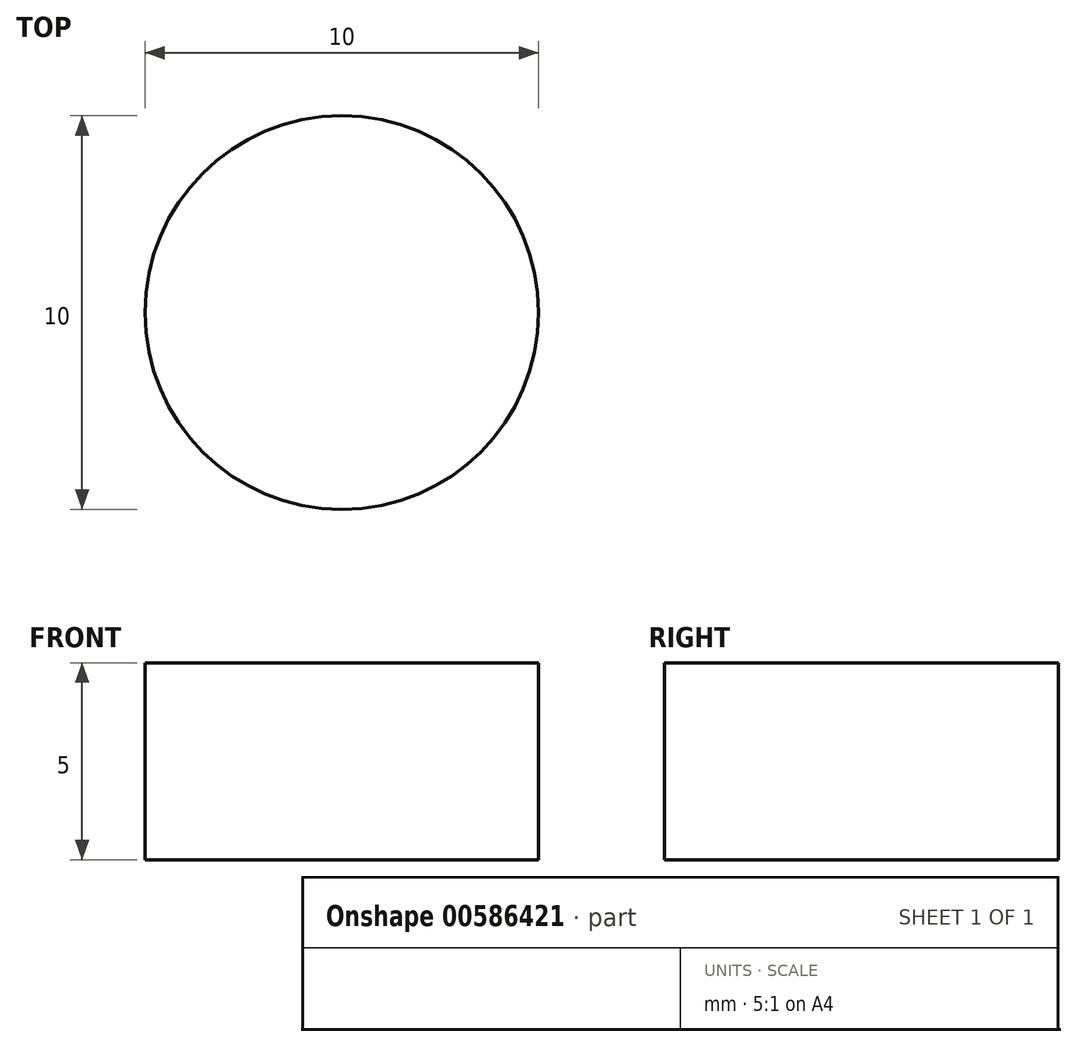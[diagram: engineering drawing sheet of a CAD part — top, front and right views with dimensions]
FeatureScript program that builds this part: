
annotation { "Feature Type Name" : "Feature", "Feature Type Description" : "" }
export const myFeature = defineFeature(function(context is Context, id is Id, definition is map)
    precondition{}
    {
        {
            var Q0;
            Q0=qCreatedBy(makeId("Top.planeOp"),FACE);
            var sketch = newSketch(context, id + "F0", { "sketchPlane" : qUnion([Q0])});
            skCircle(sketch, "E0", {"center": v(0, 0) * mm, "radius": 5 * mm});
            skSolve(sketch);
        }
        {
            var Q0;
            Q0 = qSketchRegion(id + "F0", true);
            extrude(context, id + "F1", {"entities" : qUnion([Q0]), "depth" : 5 * mm, "offsetDistance" : 25 * mm});
        }
    });
